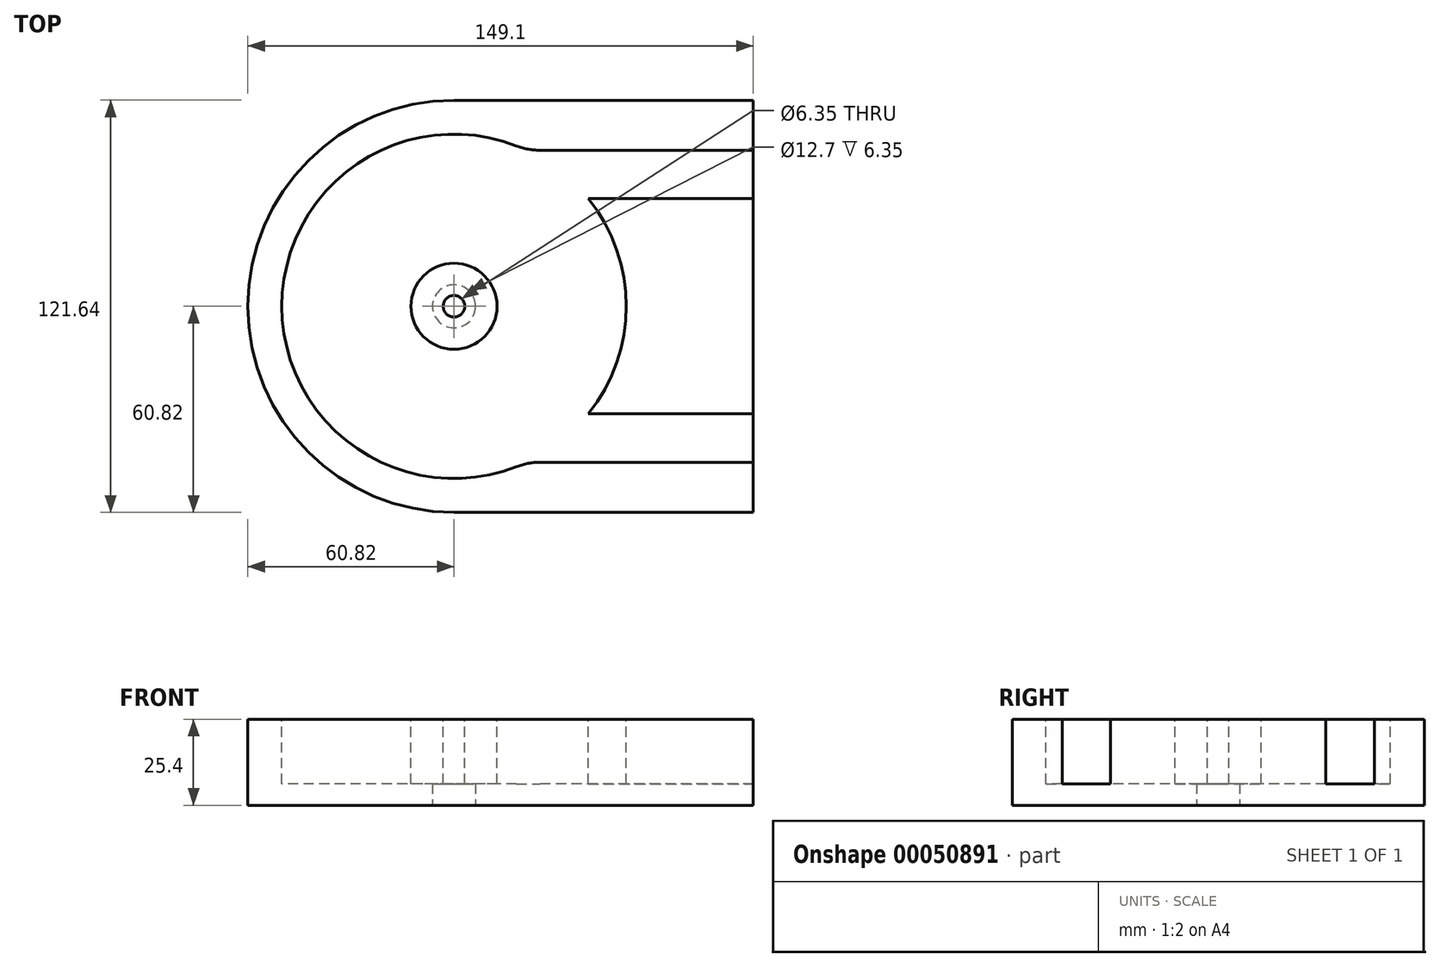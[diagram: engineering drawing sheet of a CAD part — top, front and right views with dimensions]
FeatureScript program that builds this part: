
annotation { "Feature Type Name" : "Feature", "Feature Type Description" : "" }
export const myFeature = defineFeature(function(context is Context, id is Id, definition is map)
    precondition{}
    {
        {
            var Q0;
            Q0=qCreatedBy(makeId("Top.planeOp"),FACE);
            var sketch = newSketch(context, id + "F0", { "sketchPlane" : qUnion([Q0])});
            skArc(sketch, "E0", {"start": v(0, 60.82) * mm, "mid": v(-60.82, 0) * mm, "end": v(0, -60.82) * mm});
            skLineSegment(sketch, "E1", {"start": v(0, 60.82) * mm, "end": v(88.28, 60.82) * mm});
            skLineSegment(sketch, "E2", {"start": v(88.28, 60.82) * mm, "end": v(88.28, -60.82) * mm});
            skLineSegment(sketch, "E3", {"start": v(88.28, -60.82) * mm, "end": v(0, -60.82) * mm});
            skSolve(sketch);
        }
        {
            var Q0;
            Q0=makeQuery(id+"F0.imprint","IMPRINT",FACE,{"disambiguationData":[TD([[makeQuery(id+"F0.imprint","IMPRINT",EDGE,{"derivedFrom":sQuery(id+"F0.wireOp",EDGE,"E0")}),1.0]])]});
            extrude(context, id + "F1", {"entities" : qUnion([Q0]), "depth" : 25.4 * mm});
        }
        {
            var Q0;
            Q0=makeQuery(id+"F1.opExtrude","CAP_FACE",FACE,{"disambiguationData":[OSD([sQuery(id+"F0.wireOp",EDGE,"E0"),sQuery(id+"F0.wireOp",EDGE,"E1"),sQuery(id+"F0.wireOp",EDGE,"E2"),sQuery(id+"F0.wireOp",EDGE,"E3")])],"isStart":false});
            var sketch = newSketch(context, id + "F2", { "sketchPlane" : qUnion([Q0])});
            skArc(sketch, "E4", {"start": v(21.48, 46.04) * mm, "mid": v(-50.8, 0) * mm, "end": v(21.48, -46.04) * mm});
            skCircle(sketch, "E5", {"center": v(0, 0) * mm, "radius": 12.7 * mm});
            skLineSegment(sketch, "E6", {"start": v(88.28, 46.04) * mm, "end": v(21.48, 46.04) * mm});
            skLineSegment(sketch, "E7", {"start": v(39.66, 31.75) * mm, "end": v(88.28, 31.75) * mm});
            skLineSegment(sketch, "E8", {"start": v(21.48, -46.04) * mm, "end": v(88.28, -46.04) * mm});
            skLineSegment(sketch, "E9", {"start": v(39.66, -31.75) * mm, "end": v(88.28, -31.75) * mm});
            skLineSegment(sketch, "E10", {"start": v(88.28, -31.75) * mm, "end": v(88.28, -46.04) * mm});
            skLineSegment(sketch, "E11", {"start": v(88.28, 31.75) * mm, "end": v(88.28, 46.04) * mm});
            skArc(sketch, "E12.trimOffspring", {"start": v(39.66, -31.75) * mm, "mid": v(50.8, 0) * mm, "end": v(39.66, 31.75) * mm});
            skLineSegment(sketch, "E13", {"start": v(88.28, 31.75) * mm, "end": v(88.28, -31.75) * mm, "construction": true});
            skLineSegment(sketch, "E14", {"start": v(88.28, 0) * mm, "end": v(50.8, 0) * mm, "construction": true});
            skPoint(sketch, "E14.endSnap0", {"position": v(88.28, 0) * mm});
            skCircle(sketch, "E15", {"center": v(0, 0) * mm, "radius": 3.18 * mm});
            skSolve(sketch);
        }
        {
            var Q0;
            Q0 = qSketchRegion(id + "F2", true);
            extrude(context, id + "F3", {"entities" : qUnion([Q0]), "operationType" : NewBodyOperationType.REMOVE, "oppositeDirection" : true, "depth" : 19.05 * mm});
        }
        {
            var Q0;
            Q0=makeQuery(id+"F3.boolean.opBoolean","COPY",EDGE,{"derivedFrom":makeQuery(id+"F3.opExtrude","SWEPT_EDGE",EDGE,{"disambiguationData":[OSD([sQuery(id+"F2.wireOp",EDGE,"E4"),sQuery(id+"F2.wireOp",EDGE,"E6")])]})});
            var Q1;
            Q1=makeQuery(id+"F3.boolean.opBoolean","COPY",EDGE,{"derivedFrom":makeQuery(id+"F3.opExtrude","SWEPT_EDGE",EDGE,{"disambiguationData":[OSD([sQuery(id+"F2.wireOp",EDGE,"E4"),sQuery(id+"F2.wireOp",EDGE,"E8")])]})});
            fillet(context, id + "F4", {"entities" : qUnion([Q0, Q1]), "radius" : 19.05 * mm, "tangentPropagation" : true, "allowEdgeOverflow" : false});
        }
        {
            var Q0;
            Q0=makeQuery(id+"F2.imprint","IMPRINT",FACE,{"disambiguationData":[TD([[makeQuery(id+"F2.imprint","IMPRINT",EDGE,{"derivedFrom":sQuery(id+"F2.wireOp",EDGE,"E15")}),1.0]])]});
            extrude(context, id + "F5", {"entities" : qUnion([Q0]), "operationType" : NewBodyOperationType.REMOVE, "oppositeDirection" : true, "depth" : 25.4 * mm});
        }
        {
            var Q0;
            Q0=makeQuery(id+"F1.opExtrude","CAP_FACE",FACE,{"disambiguationData":[OSD([sQuery(id+"F0.wireOp",EDGE,"E0"),sQuery(id+"F0.wireOp",EDGE,"E1"),sQuery(id+"F0.wireOp",EDGE,"E2"),sQuery(id+"F0.wireOp",EDGE,"E3")])],"isStart":true});
            var sketch = newSketch(context, id + "F6", { "sketchPlane" : qUnion([Q0])});
            skCircle(sketch, "E16", {"center": v(0, 0) * mm, "radius": 6.35 * mm});
            skSolve(sketch);
        }
        {
            var Q0;
            Q0 = qSketchRegion(id + "F6", true);
            extrude(context, id + "F7", {"entities" : qUnion([Q0]), "operationType" : NewBodyOperationType.REMOVE, "oppositeDirection" : true, "depth" : 6.35 * mm});
        }
    });
